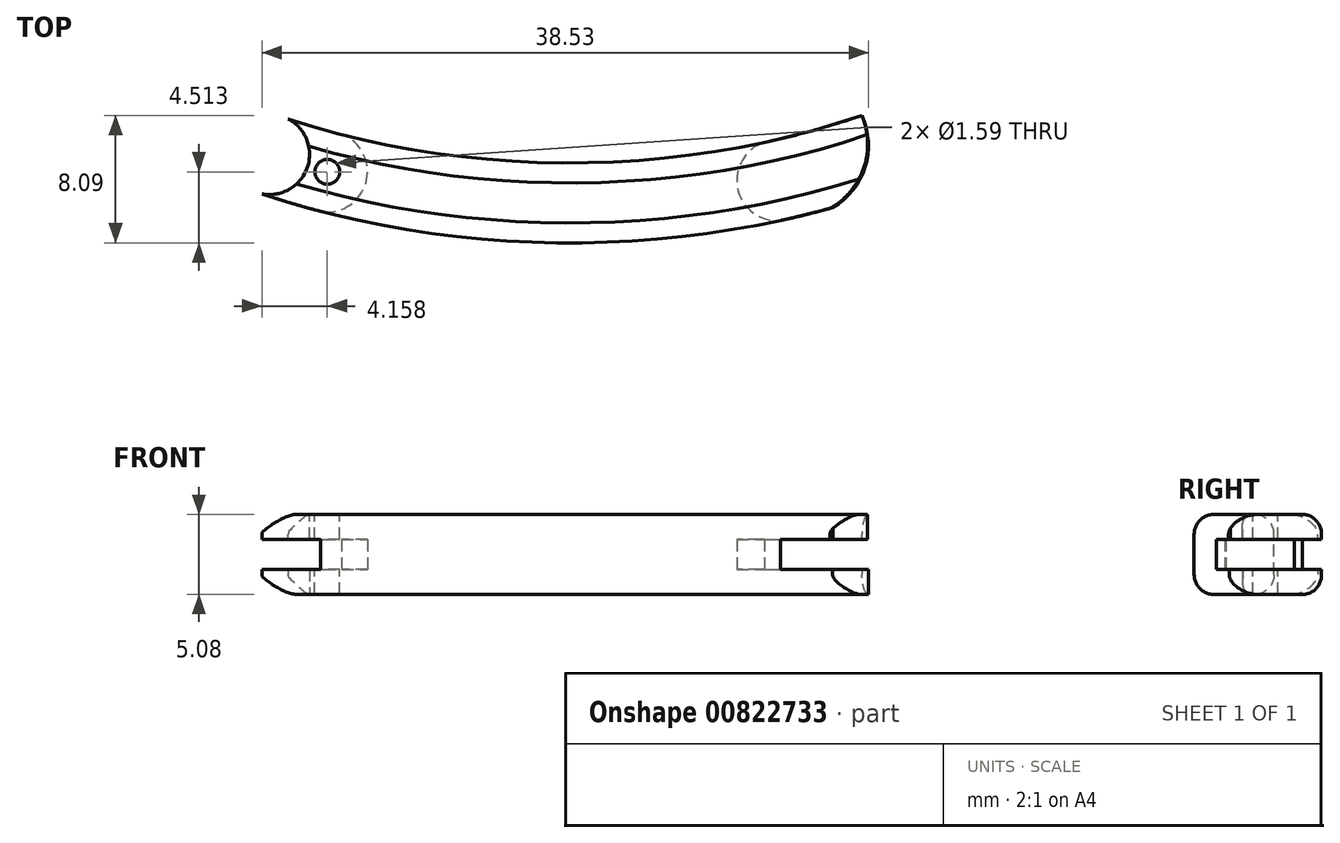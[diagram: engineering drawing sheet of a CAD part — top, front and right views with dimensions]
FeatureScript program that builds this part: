
annotation { "Feature Type Name" : "Feature", "Feature Type Description" : "" }
export const myFeature = defineFeature(function(context is Context, id is Id, definition is map)
    precondition{}
    {
        {
            var Q0;
            Q0=qCreatedBy(makeId("Top.planeOp"),FACE);
            var sketch = newSketch(context, id + "F0", { "sketchPlane" : qUnion([Q0])});
            skEllipticalArc(sketch, "E0", {});
            skEllipticalArc(sketch, "E1", {});
            skEllipticalArc(sketch, "E2", {});
            skArc(sketch, "E3", {"start": v(-15.75, -32.3) * mm, "mid": v(-12.94, -30.47) * mm, "end": v(-14.38, -27.44) * mm});
            skArc(sketch, "E4", {"start": v(12.26, -27.93) * mm, "mid": v(10.77, -31.22) * mm, "end": v(14.05, -32.72) * mm});
            const initialGuessF0  = {"E0": [0, 0, 1, 0, 0.04699, 0.03429, 5.01610929241982, 4.370671689832783], "E1": [0, 0, 1, 0, 0.04445, 0.03175, 4.9544565053868785, 4.417454356653307], "E2": [0, 0, 1, 0, 0.04191, 0.02921, 5.009210639362234, 4.362178647545779]};
            skSetInitialGuess(sketch, initialGuessF0);
            skSolve(sketch);
        }
        {
            var Q0;
            {var subQ6=sQuery(id+"F0.wireOp",EDGE,"E1");Q0=makeQuery(id+"F0.imprint","IMPRINT",FACE,{"disambiguationData":[TD([[makeQuery(id+"F0.imprint","IMPRINT",EDGE,{"derivedFrom":subQ6}),1.0]])]});}
            var Q1;
            {var subQ0=sQuery(id+"F0.wireOp",EDGE,"E1");Q1=makeQuery(id+"F0.imprint","IMPRINT",FACE,{"disambiguationData":[TD([[makeQuery(id+"F0.imprint","IMPRINT",EDGE,{"derivedFrom":subQ0}),-1.0]])]});}
            var Q2;
            {var subQ0=sQuery(id+"F0.wireOp",EDGE,"E3");var subQ1=sQuery(id+"F0.wireOp",EDGE,"E0");var subQ2=makeQuery(id+"F0.imprint","INTERSECT",VERTEX,{"disambiguationData":[OD(0.0)],"derivedFrom":[subQ1,subQ0]});Q2=makeQuery(id+"F0.imprint","IMPRINT",FACE,{"disambiguationData":[TD([[makeQuery(id+"F0.imprint","IMPRINT",EDGE,{"disambiguationData":[TD([[subQ2,-1.0]])],"derivedFrom":subQ1}),-1.0]])]});}
            var Q3;
            {var subQ0=sQuery(id+"F0.wireOp",EDGE,"E4");var subQ1=sQuery(id+"F0.wireOp",EDGE,"E0");var subQ2=makeQuery(id+"F0.imprint","INTERSECT",VERTEX,{"disambiguationData":[OD(0.0)],"derivedFrom":[subQ1,subQ0]});Q3=makeQuery(id+"F0.imprint","IMPRINT",FACE,{"disambiguationData":[TD([[makeQuery(id+"F0.imprint","IMPRINT",EDGE,{"disambiguationData":[TD([[subQ2,1.0]])],"derivedFrom":subQ1}),-1.0]])]});}
            var Q4;
            {var subQ0=sQuery(id+"F0.wireOp",EDGE,"E3");var subQ1=sQuery(id+"F0.wireOp",EDGE,"E2");var subQ2=makeQuery(id+"F0.imprint","INTERSECT",VERTEX,{"disambiguationData":[OD(0.0)],"derivedFrom":[subQ1,subQ0]});Q4=makeQuery(id+"F0.imprint","IMPRINT",FACE,{"disambiguationData":[TD([[makeQuery(id+"F0.imprint","IMPRINT",EDGE,{"disambiguationData":[TD([[subQ2,-1.0]])],"derivedFrom":subQ1}),1.0]])]});}
            extrude(context, id + "F1", {"entities" : qUnion([Q0, Q1, Q2, Q3, Q4]), "depth" : 5.08 * mm, "offsetDistance" : 25.4 * mm});
        }
        {
            var Q0;
            Q0=makeQuery(id+"F1.opExtrude","SWEPT_FACE",FACE,{"disambiguationData":[OSD([sQuery(id+"F0.wireOp",EDGE,"E2")])]});
            var Q1;
            Q1=makeQuery(id+"F1.opExtrude","SWEPT_FACE",FACE,{"disambiguationData":[OSD([sQuery(id+"F0.wireOp",EDGE,"E0")])]});
            fillet(context, id + "F2", {"entities" : qUnion([Q0, Q1]), "radius" : 1.27 * mm, "tangentPropagation" : true, "allowEdgeOverflow" : false});
        }
        {
            var Q0;
            Q0=makeQuery(id+"F1.opExtrude","CAP_FACE",FACE,{"disambiguationData":[OSD([sQuery(id+"F0.wireOp",EDGE,"E0"),sQuery(id+"F0.wireOp",EDGE,"E2"),sQuery(id+"F0.wireOp",EDGE,"E3"),sQuery(id+"F0.wireOp",EDGE,"E4")])],"isStart":false});
            var sketch = newSketch(context, id + "F3", { "sketchPlane" : qUnion([Q0])});
            skEllipticalArc(sketch, "E5", {});
            skArc(sketch, "E6", {"start": v(-19.56, -31.18) * mm, "mid": v(-16.67, -29.51) * mm, "end": v(-17.9, -26.41) * mm});
            skArc(sketch, "E7", {"start": v(16.7, -32) * mm, "mid": v(18.7, -29.44) * mm, "end": v(18.54, -26.2) * mm});
            skPoint(sketch, "E8", {"position": v(16.7, -32) * mm});
            skArc(sketch, "E9", {"start": v(-19.56, -31.18) * mm, "mid": v(-1.55, -36.8) * mm, "end": v(16.7, -32) * mm});
            const initialGuessF3  = {"E5": [0, 0, 1, 0, 0.04191, 0.02921, 4.271247218896428, 5.170681346269406]};
            skSetInitialGuess(sketch, initialGuessF3);
            skSolve(sketch);
        }
        {
            var Q0;
            Q0=qCreatedBy(makeId("Top.planeOp"),FACE);
            var sketch = newSketch(context, id + "F4", { "sketchPlane" : qUnion([Q0])});
            skEllipticalArc(sketch, "E10", {});
            skEllipticalArc(sketch, "E11", {});
            skArc(sketch, "E12", {"start": v(-19.56, -31.18) * mm, "mid": v(-16.67, -29.51) * mm, "end": v(-17.9, -26.41) * mm});
            skArc(sketch, "E13", {"start": v(16.52, -32.14) * mm, "mid": v(18.73, -29.58) * mm, "end": v(18.54, -26.2) * mm});
            const initialGuessF4  = {"E10": [0, 0, 1, 0, 0.04191, 0.02921, 4.2712472188748905, 5.170681346267891], "E11": [7.181311994251772e-05, -2.404612473681249e-05, 1, 0, 0.04699, 0.03429, 4.281351635396161, 5.070003422835694]};
            skSetInitialGuess(sketch, initialGuessF4);
            skSolve(sketch);
        }
        {
            var Q0;
            Q0 = qSketchRegion(id + "F3", true);
            extrude(context, id + "F5", {"entities" : qUnion([Q0]), "operationType" : NewBodyOperationType.REMOVE, "oppositeDirection" : true, "depth" : 1.59 * mm, "offsetDistance" : 25.4 * mm});
        }
        {
            var Q0;
            Q0 = qSketchRegion(id + "F4", true);
            extrude(context, id + "F6", {"entities" : qUnion([Q0]), "operationType" : NewBodyOperationType.REMOVE, "depth" : 1.59 * mm, "offsetDistance" : 25.4 * mm});
        }
        {
            var Q0;
            Q0=qCreatedBy(makeId("Top.planeOp"),FACE);
            var sketch = newSketch(context, id + "F7", { "sketchPlane" : qUnion([Q0])});
            skEllipse(sketch, "E14", {"center": v(0, 0) * mm, "majorRadius": 47 * mm, "minorRadius": 34.3 * mm, "majorAxis": v(1, 0)});
            skEllipse(sketch, "E15", {"center": v(0, 0) * mm, "majorRadius": 41.91 * mm, "minorRadius": 29.21 * mm, "majorAxis": v(1, 0)});
            skSolve(sketch);
        }
        {
            var Q0;
            Q0=makeQuery(id+"F7.imprint","IMPRINT",FACE,{"disambiguationData":[TD([[makeQuery(id+"F7.imprint","IMPRINT",EDGE,{"derivedFrom":sQuery(id+"F7.wireOp",EDGE,"E14")}),1.0]])]});
            extrude(context, id + "F8", {"entities" : qUnion([Q0]), "depth" : 5.08 * mm, "offsetDistance" : 25.4 * mm});
        }
        {
            var Q0;
            Q0=makeQuery(id+"F8.opExtrude","SWEPT_FACE",FACE,{"disambiguationData":[OSD([sQuery(id+"F7.wireOp",EDGE,"E14")])]});
            var Q1;
            Q1=makeQuery(id+"F8.opExtrude","SWEPT_FACE",FACE,{"disambiguationData":[OSD([sQuery(id+"F7.wireOp",EDGE,"E15")])]});
            fillet(context, id + "F9", {"entities" : qUnion([Q0, Q1]), "radius" : 1.27 * mm, "tangentPropagation" : true, "allowEdgeOverflow" : false});
        }
        {
            var Q0;
            Q0=makeQuery(id+"F1.opExtrude","SWEPT_BODY",BODY,{"disambiguationData":[OSD([sQuery(id+"F0.wireOp",EDGE,"E0"),sQuery(id+"F0.wireOp",EDGE,"E2"),sQuery(id+"F0.wireOp",EDGE,"E3"),sQuery(id+"F0.wireOp",EDGE,"E4")])]});
            var Q1;
            Q1=makeQuery(id+"F8.opExtrude","SWEPT_BODY",BODY,{"disambiguationData":[OSD([sQuery(id+"F7.wireOp",EDGE,"E14"),sQuery(id+"F7.wireOp",EDGE,"E15")])]});
            booleanBodies(context, id + "F10", {"operationType" : BooleanOperationType.SUBTRACTION, "tools" : qUnion([Q0]), "targets" : qUnion([Q1])});
        }
        {
            var Q0;
            Q0=makeQuery(id+"F8.opExtrude","CAP_FACE",FACE,{"disambiguationData":[OSD([sQuery(id+"F7.wireOp",EDGE,"E14"),sQuery(id+"F7.wireOp",EDGE,"E15")])],"isStart":false});
            var sketch = newSketch(context, id + "F11", { "sketchPlane" : qUnion([Q0])});
            skPoint(sketch, "E16.1", {"position": v(-15.4, -29.78) * mm});
            skSolve(sketch);
        }
        {
            var Q0;
            Q0=sQuery(id+"F11.wireOp",VERTEX,"E16.1");
            var Q1;
            Q1=makeQuery(id+"F8.opExtrude","SWEPT_BODY",BODY,{"disambiguationData":[OSD([sQuery(id+"F7.wireOp",EDGE,"E14"),sQuery(id+"F7.wireOp",EDGE,"E15")])]});
            hole(context, id + "F12", {"style" : HoleStyle.SIMPLE, "endStyle" : HoleEndStyle.BLIND, "holeDiameter" : 1.59 * mm, "majorDiameter" : 6.35 * mm, "holeDepth" : 7.62 * mm, "isTappedThrough" : true, "tappedDepth" : 12.7 * mm, "tapClearance" : 3, "locations" : qUnion([Q0]), "scope" : qUnion([Q1])});
        }
    });
